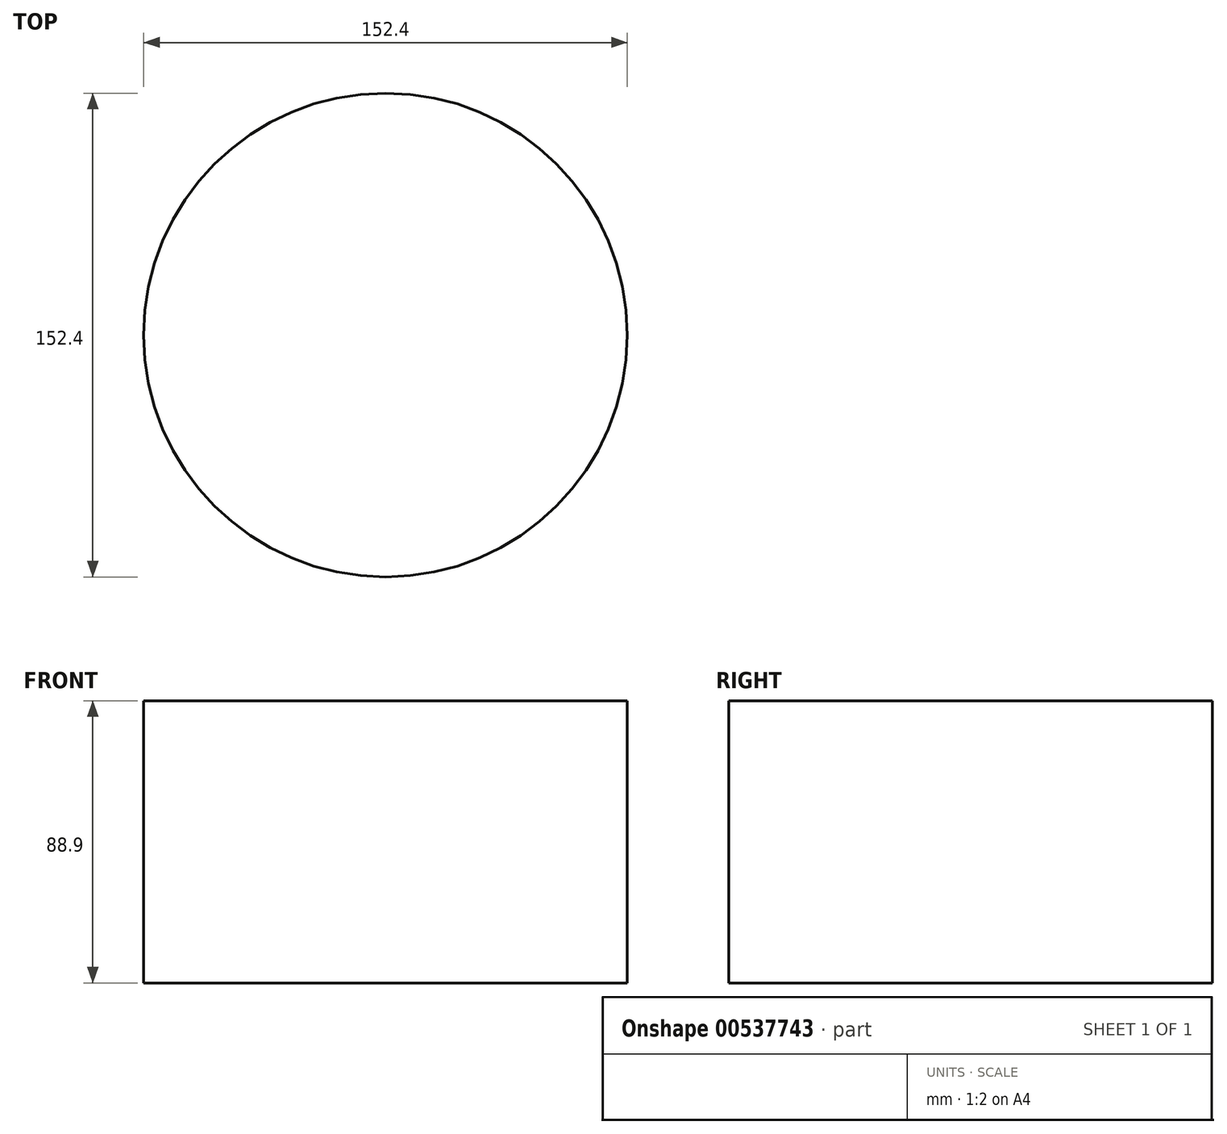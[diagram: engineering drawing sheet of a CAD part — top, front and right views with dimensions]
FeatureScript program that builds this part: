
annotation { "Feature Type Name" : "Feature", "Feature Type Description" : "" }
export const myFeature = defineFeature(function(context is Context, id is Id, definition is map)
    precondition{}
    {
        {
            var Q0;
            Q0=qCreatedBy(makeId("Top.planeOp"),FACE);
            var sketch = newSketch(context, id + "F0", { "sketchPlane" : qUnion([Q0])});
            skCircle(sketch, "E0", {"center": v(0, 0) * mm, "radius": 76.2 * mm});
            skSolve(sketch);
        }
        {
            var Q0;
            Q0 = qSketchRegion(id + "F0", true);
            extrude(context, id + "F1", {"entities" : qUnion([Q0]), "depth" : 88.9 * mm, "offsetDistance" : 25.4 * mm, "symmetric" : true});
        }
    });
